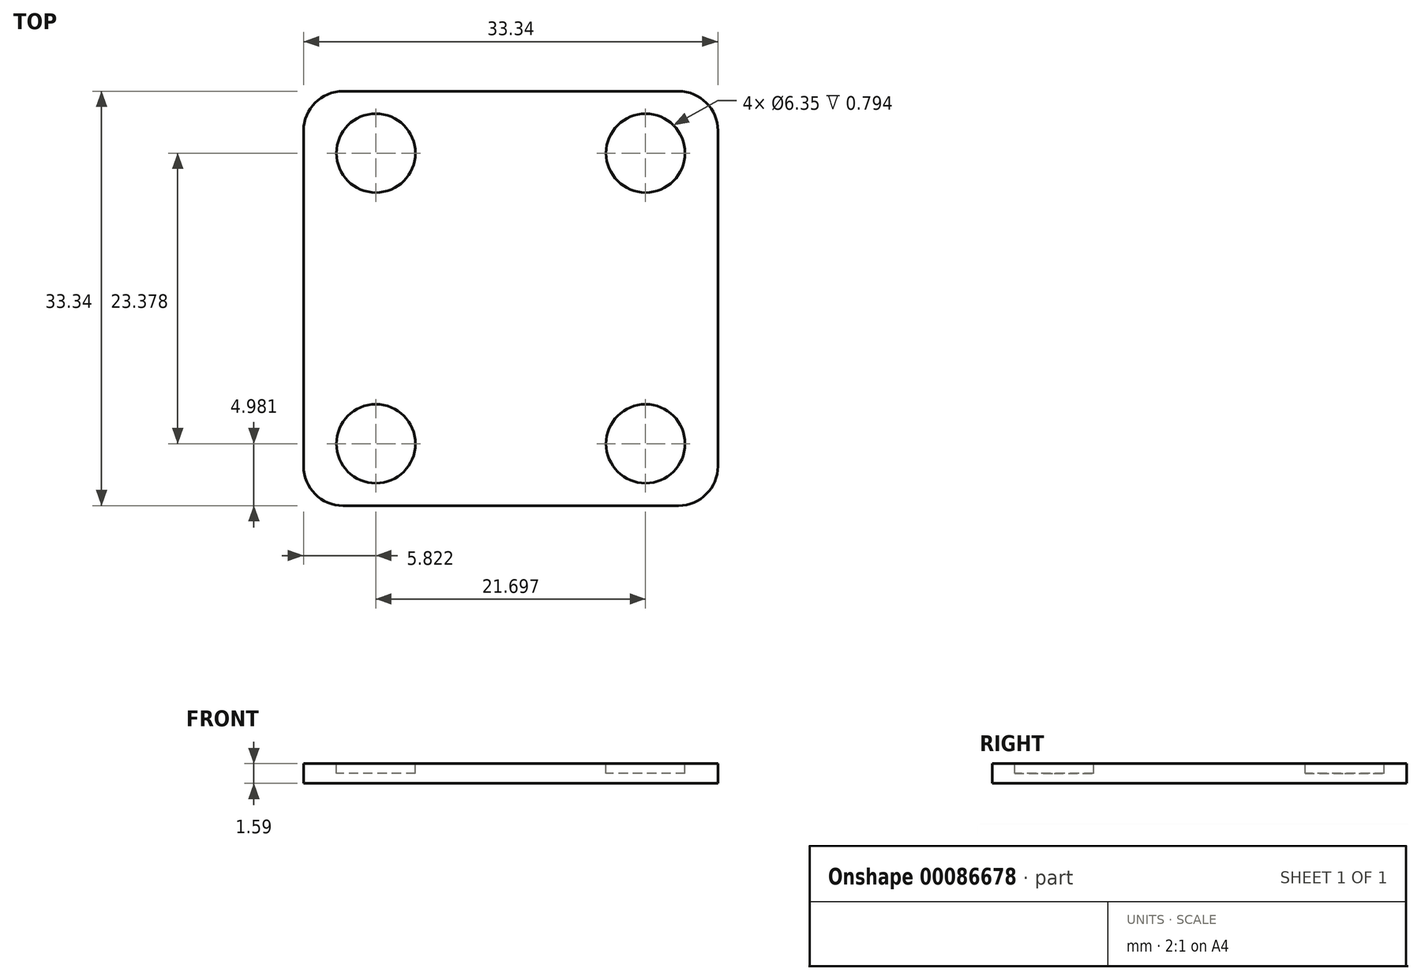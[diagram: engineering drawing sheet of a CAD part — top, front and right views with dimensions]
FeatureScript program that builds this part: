
annotation { "Feature Type Name" : "Feature", "Feature Type Description" : "" }
export const myFeature = defineFeature(function(context is Context, id is Id, definition is map)
    precondition{}
    {
        {
            var Q0;
            Q0=qCreatedBy(makeId("Top.planeOp"),FACE);
            var sketch = newSketch(context, id + "F0", { "sketchPlane" : qUnion([Q0])});
            skLineSegment(sketch, "E0.bottom", {"start": v(13.5, -16.67) * mm, "end": v(-13.5, -16.67) * mm});
            skLineSegment(sketch, "E0.top", {"start": v(13.5, 16.67) * mm, "end": v(-13.5, 16.67) * mm});
            skLineSegment(sketch, "E0.left", {"start": v(16.67, -13.5) * mm, "end": v(16.67, 13.5) * mm});
            skLineSegment(sketch, "E0.right", {"start": v(-16.67, -13.5) * mm, "end": v(-16.67, 13.5) * mm});
            skPoint(sketch, "E0.middle", {"position": v(0, 0) * mm});
            skPoint(sketch, "E1.visualSharp", {"position": v(-16.67, 16.67) * mm});
            skArc(sketch, "E1.filletArc", {"start": v(-13.5, 16.67) * mm, "mid": v(-15.74, 15.74) * mm, "end": v(-16.67, 13.5) * mm});
            skPoint(sketch, "E2.visualSharp", {"position": v(16.67, 16.67) * mm});
            skArc(sketch, "E2.filletArc", {"start": v(16.67, 13.5) * mm, "mid": v(15.74, 15.74) * mm, "end": v(13.5, 16.67) * mm});
            skPoint(sketch, "E3.visualSharp", {"position": v(16.67, -16.67) * mm});
            skArc(sketch, "E3.filletArc", {"start": v(13.5, -16.67) * mm, "mid": v(15.74, -15.74) * mm, "end": v(16.67, -13.5) * mm});
            skPoint(sketch, "E4.visualSharp", {"position": v(-16.67, -16.67) * mm});
            skArc(sketch, "E4.filletArc", {"start": v(-16.67, -13.5) * mm, "mid": v(-15.74, -15.74) * mm, "end": v(-13.5, -16.67) * mm});
            skSolve(sketch);
        }
        {
            var Q0;
            Q0=makeQuery(id+"F0.imprint","IMPRINT",FACE,{"disambiguationData":[TD([[makeQuery(id+"F0.imprint","IMPRINT",EDGE,{"derivedFrom":sQuery(id+"F0.wireOp",EDGE,"E0.bottom")}),-1.0]])]});
            extrude(context, id + "F1", {"entities" : qUnion([Q0]), "depth" : 1.59 * mm});
        }
        {
            var Q0;
            Q0=makeQuery(id+"F1.opExtrude","CAP_FACE",FACE,{"disambiguationData":[OSD([sQuery(id+"F0.wireOp",EDGE,"E0.bottom"),sQuery(id+"F0.wireOp",EDGE,"E0.top"),sQuery(id+"F0.wireOp",EDGE,"E0.left"),sQuery(id+"F0.wireOp",EDGE,"E0.right"),sQuery(id+"F0.wireOp",EDGE,"E1.filletArc"),sQuery(id+"F0.wireOp",EDGE,"E2.filletArc"),sQuery(id+"F0.wireOp",EDGE,"E3.filletArc"),sQuery(id+"F0.wireOp",EDGE,"E4.filletArc")])],"isStart":false});
            var sketch = newSketch(context, id + "F2", { "sketchPlane" : qUnion([Q0])});
            skLineSegment(sketch, "E5.bottom", {"start": v(10.85, -11.69) * mm, "end": v(-10.85, -11.69) * mm, "construction": true});
            skLineSegment(sketch, "E5.top", {"start": v(10.85, 11.69) * mm, "end": v(-10.85, 11.69) * mm, "construction": true});
            skLineSegment(sketch, "E5.left", {"start": v(10.85, -11.69) * mm, "end": v(10.85, 11.69) * mm, "construction": true});
            skLineSegment(sketch, "E5.right", {"start": v(-10.85, -11.69) * mm, "end": v(-10.85, 11.69) * mm, "construction": true});
            skPoint(sketch, "E5.middle", {"position": v(0, 0) * mm});
            skCircle(sketch, "E6", {"center": v(-10.85, 11.69) * mm, "radius": 3.18 * mm});
            skCircle(sketch, "E7", {"center": v(10.85, 11.69) * mm, "radius": 3.18 * mm});
            skCircle(sketch, "E8", {"center": v(10.85, -11.69) * mm, "radius": 3.18 * mm});
            skCircle(sketch, "E9", {"center": v(-10.85, -11.69) * mm, "radius": 3.18 * mm});
            skSolve(sketch);
        }
        {
            var Q0;
            Q0 = qSketchRegion(id + "F2", true);
            extrude(context, id + "F3", {"entities" : qUnion([Q0]), "operationType" : NewBodyOperationType.REMOVE, "oppositeDirection" : true, "depth" : 0.8 * mm});
        }
    });
